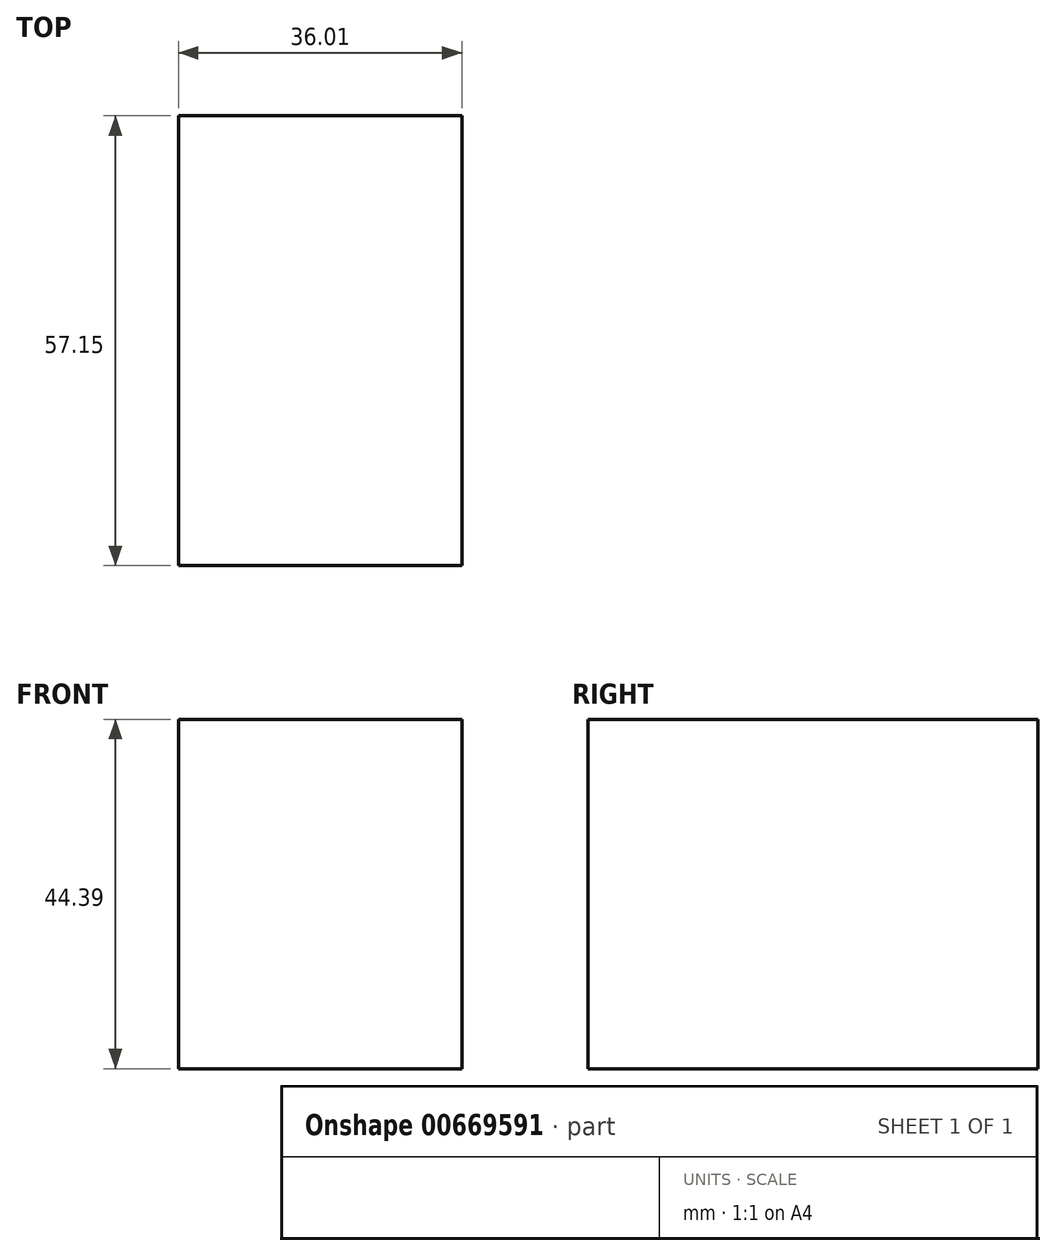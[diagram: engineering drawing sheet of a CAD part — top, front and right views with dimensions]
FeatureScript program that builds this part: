
annotation { "Feature Type Name" : "Feature", "Feature Type Description" : "" }
export const myFeature = defineFeature(function(context is Context, id is Id, definition is map)
    precondition{}
    {
        {
            var Q0;
            Q0=qCreatedBy(makeId("Front.planeOp"),FACE);
            var sketch = newSketch(context, id + "F0", { "sketchPlane" : qUnion([Q0])});
            skLineSegment(sketch, "E0.bottom", {"start": v(0, 0) * mm, "end": v(36, 0) * mm});
            skLineSegment(sketch, "E0.top", {"start": v(0, -44.4) * mm, "end": v(36, -44.4) * mm});
            skLineSegment(sketch, "E0.left", {"start": v(0, 0) * mm, "end": v(0, -44.4) * mm});
            skLineSegment(sketch, "E0.right", {"start": v(36, 0) * mm, "end": v(36, -44.4) * mm});
            skSolve(sketch);
        }
        {
            var Q0;
            Q0 = qSketchRegion(id + "F0", true);
            extrude(context, id + "F1", {"entities" : qUnion([Q0]), "depth" : 57.15 * mm, "offsetDistance" : 25.4 * mm});
        }
    });
